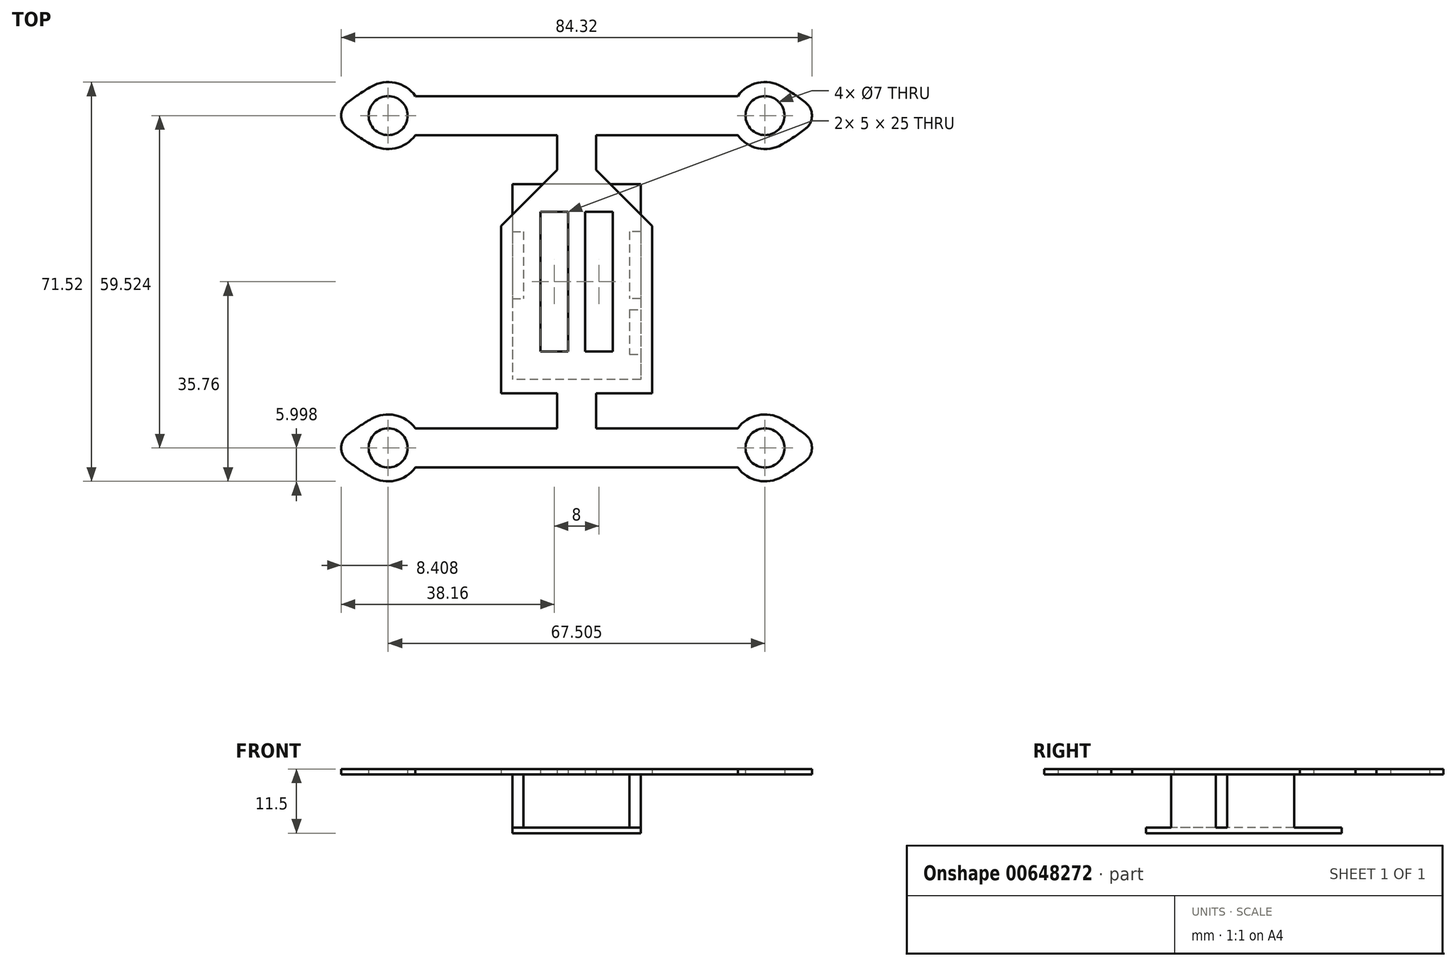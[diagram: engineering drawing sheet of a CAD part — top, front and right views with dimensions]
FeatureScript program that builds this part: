
annotation { "Feature Type Name" : "Feature", "Feature Type Description" : "" }
export const myFeature = defineFeature(function(context is Context, id is Id, definition is map)
    precondition{}
    {
        {
            var Q0;
            Q0=qCreatedBy(makeId("Top.planeOp"),FACE);
            var sketch = newSketch(context, id + "F0", { "sketchPlane" : qUnion([Q0])});
            skLineSegment(sketch, "E0.bottom", {"start": v(-33.75, 29.76) * mm, "end": v(33.75, 29.76) * mm, "construction": true});
            skLineSegment(sketch, "E0.top", {"start": v(-33.75, -29.76) * mm, "end": v(33.75, -29.76) * mm, "construction": true});
            skLineSegment(sketch, "E0.left", {"start": v(-33.75, 29.76) * mm, "end": v(-33.75, -29.76) * mm, "construction": true});
            skLineSegment(sketch, "E0.right", {"start": v(33.75, 29.76) * mm, "end": v(33.75, -29.76) * mm, "construction": true});
            skPoint(sketch, "E0.middle", {"position": v(0, 0) * mm});
            skLineSegment(sketch, "E1.left", {"start": v(-13.5, 10) * mm, "end": v(-13.5, -20) * mm});
            skCircle(sketch, "E2", {"center": v(-33.75, 29.76) * mm, "radius": 3.5 * mm});
            skArc(sketch, "E3", {"start": v(-28.88, 33.26) * mm, "mid": v(-32.49, 35.63) * mm, "end": v(-36.75, 34.96) * mm});
            skCircle(sketch, "E4.MirrorC", {"center": v(33.75, 29.76) * mm, "radius": 3.5 * mm});
            skArc(sketch, "E5.MirrorC", {"start": v(-36.75, -24.57) * mm, "mid": v(-32.49, -23.9) * mm, "end": v(-28.88, -26.26) * mm});
            skCircle(sketch, "E6.MirrorC", {"center": v(-33.75, -29.76) * mm, "radius": 3.5 * mm});
            skCircle(sketch, "E7.MirrorC", {"center": v(33.75, -29.76) * mm, "radius": 3.5 * mm});
            skLineSegment(sketch, "E8", {"start": v(-28.88, 26.26) * mm, "end": v(-3.5, 26.26) * mm});
            skLineSegment(sketch, "E9", {"start": v(-3.5, 26.26) * mm, "end": v(-3.5, 20) * mm});
            skLineSegment(sketch, "E10.MirrorCS", {"start": v(-28.88, -26.26) * mm, "end": v(-3.5, -26.26) * mm});
            skLineSegment(sketch, "E11.MirrorCS", {"start": v(-3.5, -26.26) * mm, "end": v(-3.5, -20) * mm});
            skLineSegment(sketch, "E12.MirrorCS", {"start": v(28.88, 26.26) * mm, "end": v(3.5, 26.26) * mm});
            skLineSegment(sketch, "E13.MirrorCS", {"start": v(3.5, 26.26) * mm, "end": v(3.5, 20) * mm});
            skLineSegment(sketch, "E14.MirrorCS", {"start": v(3.5, -26.26) * mm, "end": v(3.5, -20) * mm});
            skLineSegment(sketch, "E15.MirrorCS", {"start": v(28.88, -26.26) * mm, "end": v(3.5, -26.26) * mm});
            skLineSegment(sketch, "E16.bottom", {"start": v(-6.5, 12.5) * mm, "end": v(-1.5, 12.5) * mm});
            skLineSegment(sketch, "E16.top", {"start": v(-6.5, -12.5) * mm, "end": v(-1.5, -12.5) * mm});
            skLineSegment(sketch, "E16.left", {"start": v(-6.5, 12.5) * mm, "end": v(-6.5, -12.5) * mm});
            skLineSegment(sketch, "E16.right", {"start": v(-1.5, 12.5) * mm, "end": v(-1.5, -12.5) * mm});
            skLineSegment(sketch, "E17.MirrorCS", {"start": v(1.5, 12.5) * mm, "end": v(1.5, -12.5) * mm});
            skLineSegment(sketch, "E18.MirrorCS", {"start": v(6.5, 12.5) * mm, "end": v(6.5, -12.5) * mm});
            skLineSegment(sketch, "E19.MirrorCS", {"start": v(6.5, -12.5) * mm, "end": v(1.5, -12.5) * mm});
            skLineSegment(sketch, "E20.MirrorCS", {"start": v(6.5, 12.5) * mm, "end": v(1.5, 12.5) * mm});
            skLineSegment(sketch, "E21", {"start": v(0, 77.3) * mm, "end": v(0, 0) * mm, "construction": true});
            skLineSegment(sketch, "E22", {"start": v(0, 0) * mm, "end": v(80.47, 0) * mm, "construction": true});
            skArc(sketch, "E23.MirrorC", {"start": v(28.88, 33.26) * mm, "mid": v(32.49, 35.63) * mm, "end": v(36.75, 34.96) * mm});
            skArc(sketch, "E24.MirrorC", {"start": v(36.75, -24.57) * mm, "mid": v(32.49, -23.9) * mm, "end": v(28.88, -26.26) * mm});
            skLineSegment(sketch, "E25", {"start": v(-28.88, 33.26) * mm, "end": v(28.88, 33.26) * mm});
            skLineSegment(sketch, "E26.MirrorCS", {"start": v(-28.88, -33.26) * mm, "end": v(28.88, -33.26) * mm});
            skArc(sketch, "E27", {"start": v(-36.75, 34.96) * mm, "mid": v(-38.9, 33.62) * mm, "end": v(-40.97, 32.15) * mm});
            skArc(sketch, "E28", {"start": v(-40.97, 27.37) * mm, "mid": v(-38.9, 25.9) * mm, "end": v(-36.75, 24.57) * mm});
            skArc(sketch, "E29.filletArc", {"start": v(-40.97, 32.15) * mm, "mid": v(-42.16, 29.76) * mm, "end": v(-40.97, 27.37) * mm});
            skArc(sketch, "E30.MirrorCS", {"start": v(36.75, 34.96) * mm, "mid": v(38.9, 33.62) * mm, "end": v(40.97, 32.15) * mm});
            skArc(sketch, "E31.MirrorCS", {"start": v(40.97, 32.15) * mm, "mid": v(42.16, 29.76) * mm, "end": v(40.97, 27.37) * mm});
            skArc(sketch, "E32.MirrorCS", {"start": v(40.97, 27.37) * mm, "mid": v(38.9, 25.9) * mm, "end": v(36.75, 24.57) * mm});
            skArc(sketch, "E33.MirrorCS", {"start": v(36.75, -34.96) * mm, "mid": v(38.9, -33.62) * mm, "end": v(40.97, -32.15) * mm});
            skArc(sketch, "E34.MirrorCS", {"start": v(40.97, -32.15) * mm, "mid": v(42.16, -29.76) * mm, "end": v(40.97, -27.37) * mm});
            skArc(sketch, "E35.MirrorCS", {"start": v(40.97, -27.37) * mm, "mid": v(38.9, -25.9) * mm, "end": v(36.75, -24.57) * mm});
            skArc(sketch, "E36.MirrorCS", {"start": v(-40.97, -27.37) * mm, "mid": v(-38.9, -25.9) * mm, "end": v(-36.75, -24.57) * mm});
            skArc(sketch, "E37.MirrorCS", {"start": v(-40.97, -32.15) * mm, "mid": v(-42.16, -29.76) * mm, "end": v(-40.97, -27.37) * mm});
            skArc(sketch, "E38.MirrorCS", {"start": v(-36.75, -34.96) * mm, "mid": v(-38.9, -33.62) * mm, "end": v(-40.97, -32.15) * mm});
            skArc(sketch, "E39.trimOffspring", {"start": v(36.75, 24.57) * mm, "mid": v(32.49, 23.9) * mm, "end": v(28.88, 26.26) * mm});
            skArc(sketch, "E40.trimOffspring", {"start": v(-36.75, 24.57) * mm, "mid": v(-32.49, 23.9) * mm, "end": v(-28.88, 26.26) * mm});
            skArc(sketch, "E41.trimOffspring", {"start": v(28.88, -33.26) * mm, "mid": v(32.49, -35.63) * mm, "end": v(36.75, -34.96) * mm});
            skArc(sketch, "E42.trimOffspring", {"start": v(-28.88, -33.26) * mm, "mid": v(-32.49, -35.63) * mm, "end": v(-36.75, -34.96) * mm});
            skPoint(sketch, "E43.endSnap0", {"position": v(-4, 12.5) * mm});
            skPoint(sketch, "E44.orphan", {"position": v(13.5, 20) * mm});
            skPoint(sketch, "E45.trimOffspring.end.orphan", {"position": v(13.5, -20) * mm});
            skLineSegment(sketch, "E46", {"start": v(-13.5, -20) * mm, "end": v(-3.5, -20) * mm});
            skLineSegment(sketch, "E47", {"start": v(13.5, 10) * mm, "end": v(13.5, -20) * mm, "construction": true});
            skLineSegment(sketch, "E48.trimOffspring", {"start": v(3.5, -20) * mm, "end": v(13.5, -20) * mm});
            skLineSegment(sketch, "E49", {"start": v(13.5, 10) * mm, "end": v(13.5, -20) * mm});
            skLineSegment(sketch, "E50", {"start": v(-3.5, 20) * mm, "end": v(-13.5, 10) * mm});
            skLineSegment(sketch, "E51.MirrorCS", {"start": v(3.5, 20) * mm, "end": v(13.5, 10) * mm});
            skPoint(sketch, "E1.bottom.start.orphan", {"position": v(-13.5, 20) * mm});
            skSolve(sketch);
        }
        {
            var Q0;
            Q0 = qSketchRegion(id + "F0", true);
            extrude(context, id + "F1", {"entities" : qUnion([Q0]), "depth" : 1 * mm, "offsetDistance" : 25 * mm});
        }
        {
            var Q0;
            Q0=qCreatedBy(makeId("Top.planeOp"),FACE);
            var sketch = newSketch(context, id + "F2", { "sketchPlane" : qUnion([Q0])});
            skLineSegment(sketch, "E52.bottom", {"start": v(-11.5, 20.55) * mm, "end": v(11.5, 20.55) * mm, "construction": true});
            skLineSegment(sketch, "E52.top", {"start": v(-11.5, -20.55) * mm, "end": v(11.5, -20.55) * mm, "construction": true});
            skLineSegment(sketch, "E52.left", {"start": v(-11.5, 20.55) * mm, "end": v(-11.5, -20.55) * mm, "construction": true});
            skLineSegment(sketch, "E52.right", {"start": v(11.5, 20.55) * mm, "end": v(11.5, -20.55) * mm, "construction": true});
            skPoint(sketch, "E52.middle", {"position": v(0, 0) * mm});
            skLineSegment(sketch, "E53", {"start": v(0, 20.79) * mm, "end": v(0, 0) * mm, "construction": true});
            skLineSegment(sketch, "E54", {"start": v(0, 0) * mm, "end": v(21.02, 0) * mm, "construction": true});
            skLineSegment(sketch, "E55.bottom", {"start": v(-11.5, 9) * mm, "end": v(-9.5, 9) * mm});
            skLineSegment(sketch, "E55.top", {"start": v(-11.5, -3) * mm, "end": v(-9.5, -3) * mm});
            skLineSegment(sketch, "E55.left", {"start": v(-11.5, 9) * mm, "end": v(-11.5, -3) * mm});
            skLineSegment(sketch, "E55.right", {"start": v(-9.5, 9) * mm, "end": v(-9.5, -3) * mm});
            skLineSegment(sketch, "E56.MirrorCS", {"start": v(11.5, 9) * mm, "end": v(9.5, 9) * mm});
            skLineSegment(sketch, "E57.MirrorCS", {"start": v(11.5, 9) * mm, "end": v(11.5, -3) * mm});
            skLineSegment(sketch, "E58.MirrorCS", {"start": v(11.5, -3) * mm, "end": v(9.5, -3) * mm});
            skLineSegment(sketch, "E59", {"start": v(9.5, 9) * mm, "end": v(9.5, -3) * mm});
            skLineSegment(sketch, "E60.bottom", {"start": v(9.5, -5) * mm, "end": v(11.5, -5) * mm});
            skLineSegment(sketch, "E60.top", {"start": v(9.5, -13) * mm, "end": v(11.5, -13) * mm});
            skLineSegment(sketch, "E60.left", {"start": v(9.5, -5) * mm, "end": v(9.5, -13) * mm});
            skLineSegment(sketch, "E60.right", {"start": v(11.5, -5) * mm, "end": v(11.5, -13) * mm});
            skSolve(sketch);
        }
        {
            var Q0;
            Q0=makeQuery(id+"F2.imprint","IMPRINT",FACE,{"disambiguationData":[TD([[makeQuery(id+"F2.imprint","IMPRINT",EDGE,{"derivedFrom":sQuery(id+"F2.wireOp",EDGE,"E60.bottom")}),-1.0]])]});
            var Q1;
            Q1=makeQuery(id+"F2.imprint","IMPRINT",FACE,{"disambiguationData":[TD([[makeQuery(id+"F2.imprint","IMPRINT",EDGE,{"derivedFrom":sQuery(id+"F2.wireOp",EDGE,"E56.MirrorCS")}),1.0]])]});
            var Q2;
            Q2=makeQuery(id+"F2.imprint","IMPRINT",FACE,{"disambiguationData":[TD([[makeQuery(id+"F2.imprint","IMPRINT",EDGE,{"derivedFrom":sQuery(id+"F2.wireOp",EDGE,"E55.bottom")}),-1.0]])]});
            extrude(context, id + "F3", {"entities" : qUnion([Q0, Q1, Q2]), "operationType" : NewBodyOperationType.ADD, "oppositeDirection" : true, "depth" : 9.5 * mm, "offsetDistance" : 25 * mm});
        }
        {
            var Q0;
            Q0=makeQuery(id+"F3.opExtrude","CAP_FACE",FACE,{"disambiguationData":[OSD([sQuery(id+"F2.wireOp",EDGE,"E60.bottom"),sQuery(id+"F2.wireOp",EDGE,"E60.top"),sQuery(id+"F2.wireOp",EDGE,"E60.left"),sQuery(id+"F2.wireOp",EDGE,"E60.right")])],"isStart":false});
            var sketch = newSketch(context, id + "F4", { "sketchPlane" : qUnion([Q0])});
            skLineSegment(sketch, "E61.bottom", {"start": v(11.5, -17.5) * mm, "end": v(-11.5, -17.5) * mm});
            skLineSegment(sketch, "E61.top", {"start": v(11.5, 17.5) * mm, "end": v(-11.5, 17.5) * mm});
            skLineSegment(sketch, "E61.left", {"start": v(11.5, -17.5) * mm, "end": v(11.5, 17.5) * mm});
            skLineSegment(sketch, "E61.right", {"start": v(-11.5, -17.5) * mm, "end": v(-11.5, 17.5) * mm});
            skPoint(sketch, "E61.middle", {"position": v(0, 0) * mm});
            skSolve(sketch);
        }
        {
            var Q0;
            Q0 = qSketchRegion(id + "F4", true);
            extrude(context, id + "F5", {"entities" : qUnion([Q0]), "operationType" : NewBodyOperationType.ADD, "depth" : 1 * mm, "offsetDistance" : 25 * mm});
        }
    });
